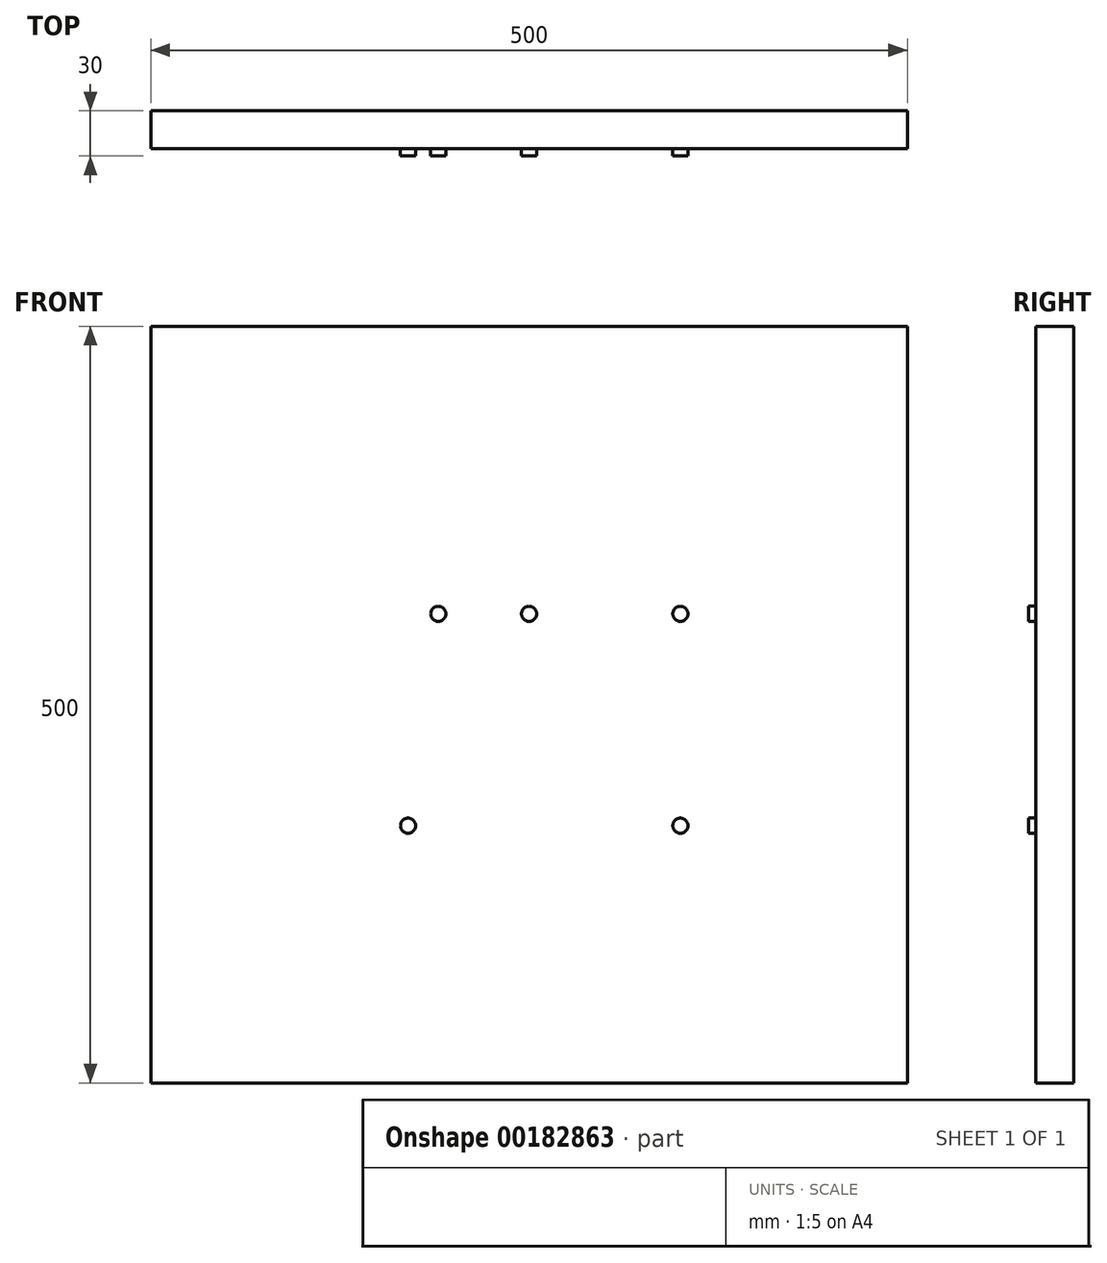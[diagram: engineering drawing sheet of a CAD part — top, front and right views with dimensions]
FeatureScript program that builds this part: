
annotation { "Feature Type Name" : "Feature", "Feature Type Description" : "" }
export const myFeature = defineFeature(function(context is Context, id is Id, definition is map)
    precondition{}
    {
        {
            var Q0;
            Q0=qCreatedBy(makeId("Front.planeOp"),FACE);
            var sketch = newSketch(context, id + "F0", { "sketchPlane" : qUnion([Q0])});
            skLineSegment(sketch, "E0.bottom", {"start": v(250, 250) * mm, "end": v(-250, 250) * mm});
            skLineSegment(sketch, "E0.top", {"start": v(250, -250) * mm, "end": v(-250, -250) * mm});
            skLineSegment(sketch, "E0.left", {"start": v(250, 250) * mm, "end": v(250, -250) * mm});
            skLineSegment(sketch, "E0.right", {"start": v(-250, 250) * mm, "end": v(-250, -250) * mm});
            skPoint(sketch, "E0.middle", {"position": v(0, 0) * mm});
            skSolve(sketch);
        }
        {
            var Q0;
            Q0=makeQuery(id+"F0.imprint","IMPRINT",FACE,{"disambiguationData":[TD([[makeQuery(id+"F0.imprint","IMPRINT",EDGE,{"derivedFrom":sQuery(id+"F0.wireOp",EDGE,"E0.bottom")}),1.0]])]});
            extrude(context, id + "F1", {"entities" : qUnion([Q0]), "depth" : 25 * mm});
        }
        {
            var Q0;
            Q0=makeQuery(id+"F1.opExtrude","CAP_FACE",FACE,{"disambiguationData":[OSD([sQuery(id+"F0.wireOp",EDGE,"E0.bottom"),sQuery(id+"F0.wireOp",EDGE,"E0.top"),sQuery(id+"F0.wireOp",EDGE,"E0.left"),sQuery(id+"F0.wireOp",EDGE,"E0.right")])],"isStart":false});
            var sketch = newSketch(context, id + "F2", { "sketchPlane" : qUnion([Q0])});
            skCircle(sketch, "E1", {"center": v(-60, 60) * mm, "radius": 5 * mm});
            skCircle(sketch, "E2", {"center": v(0, 60) * mm, "radius": 5 * mm});
            skCircle(sketch, "E3", {"center": v(100, 60) * mm, "radius": 5 * mm});
            skCircle(sketch, "E4", {"center": v(100, -80) * mm, "radius": 5 * mm});
            skCircle(sketch, "E5", {"center": v(-80, -80) * mm, "radius": 5 * mm});
            skSolve(sketch);
        }
        {
            var Q0;
            Q0 = qSketchRegion(id + "F2", true);
            extrude(context, id + "F3", {"entities" : qUnion([Q0]), "operationType" : NewBodyOperationType.ADD, "depth" : 5 * mm});
        }
    });
